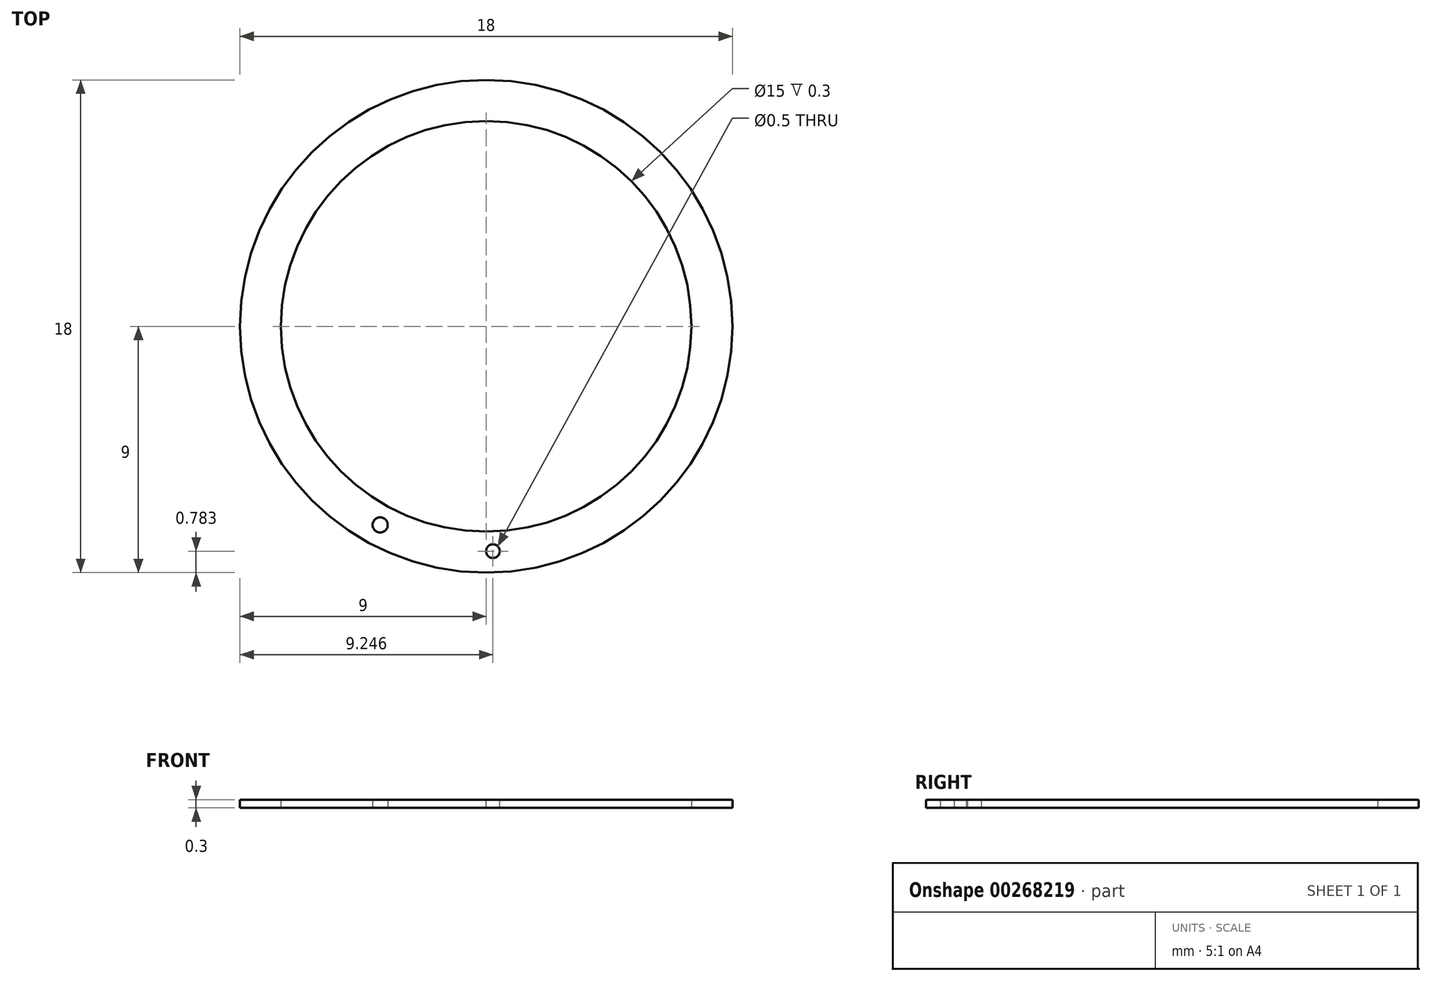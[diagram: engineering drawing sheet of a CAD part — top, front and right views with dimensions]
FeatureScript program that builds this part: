
annotation { "Feature Type Name" : "Feature", "Feature Type Description" : "" }
export const myFeature = defineFeature(function(context is Context, id is Id, definition is map)
    precondition{}
    {
        {
            var Q0;
            Q0=qCreatedBy(makeId("Top.planeOp"),FACE);
            var sketch = newSketch(context, id + "F0", { "sketchPlane" : qUnion([Q0])});
            skCircle(sketch, "E0", {"center": v(0, 0) * mm, "radius": 9 * mm});
            skCircle(sketch, "E1", {"center": v(0, 0) * mm, "radius": 7.5 * mm});
            skLineSegment(sketch, "E2", {"start": v(0, 0) * mm, "end": v(-5.32, -10.07) * mm});
            skSolve(sketch);
        }
        {
            var Q0;
            Q0=makeQuery(id+"F0.imprint","IMPRINT",FACE,{"disambiguationData":[TD([[makeQuery(id+"F0.imprint","IMPRINT",EDGE,{"derivedFrom":sQuery(id+"F0.wireOp",EDGE,"E1")}),1.0]])]});
            var sketch = newSketch(context, id + "F1", { "sketchPlane" : qUnion([Q0])});
            skCircle(sketch, "E3", {"center": v(-3.88, -7.26) * mm, "radius": 0.28 * mm});
            skCircle(sketch, "E4", {"center": v(0.25, -8.22) * mm, "radius": 0.25 * mm});
            skSolve(sketch);
        }
        {
            var Q0;
            Q0 = qSketchRegion(id + "F1", true);
            var Q1;
            Q1=makeQuery(id+"F0.imprint","IMPRINT",FACE,{"disambiguationData":[TD([[makeQuery(id+"F0.imprint","IMPRINT",EDGE,{"derivedFrom":sQuery(id+"F0.wireOp",EDGE,"E0")}),1.0]])]});
            extrude(context, id + "F2", {"entities" : qUnion([Q0, Q1]), "depth" : 0.3 * mm});
        }
        {
            var Q0;
            Q0=makeQuery(id+"F2.opExtrude","CAP_FACE",FACE,{"disambiguationData":[OSD([sQuery(id+"F1.wireOp",EDGE,"E4")])],"isStart":false});
            extrude(context, id + "F3", {"entities" : qUnion([Q0]), "operationType" : NewBodyOperationType.REMOVE, "oppositeDirection" : true, "depth" : 25 * mm});
        }
    });
